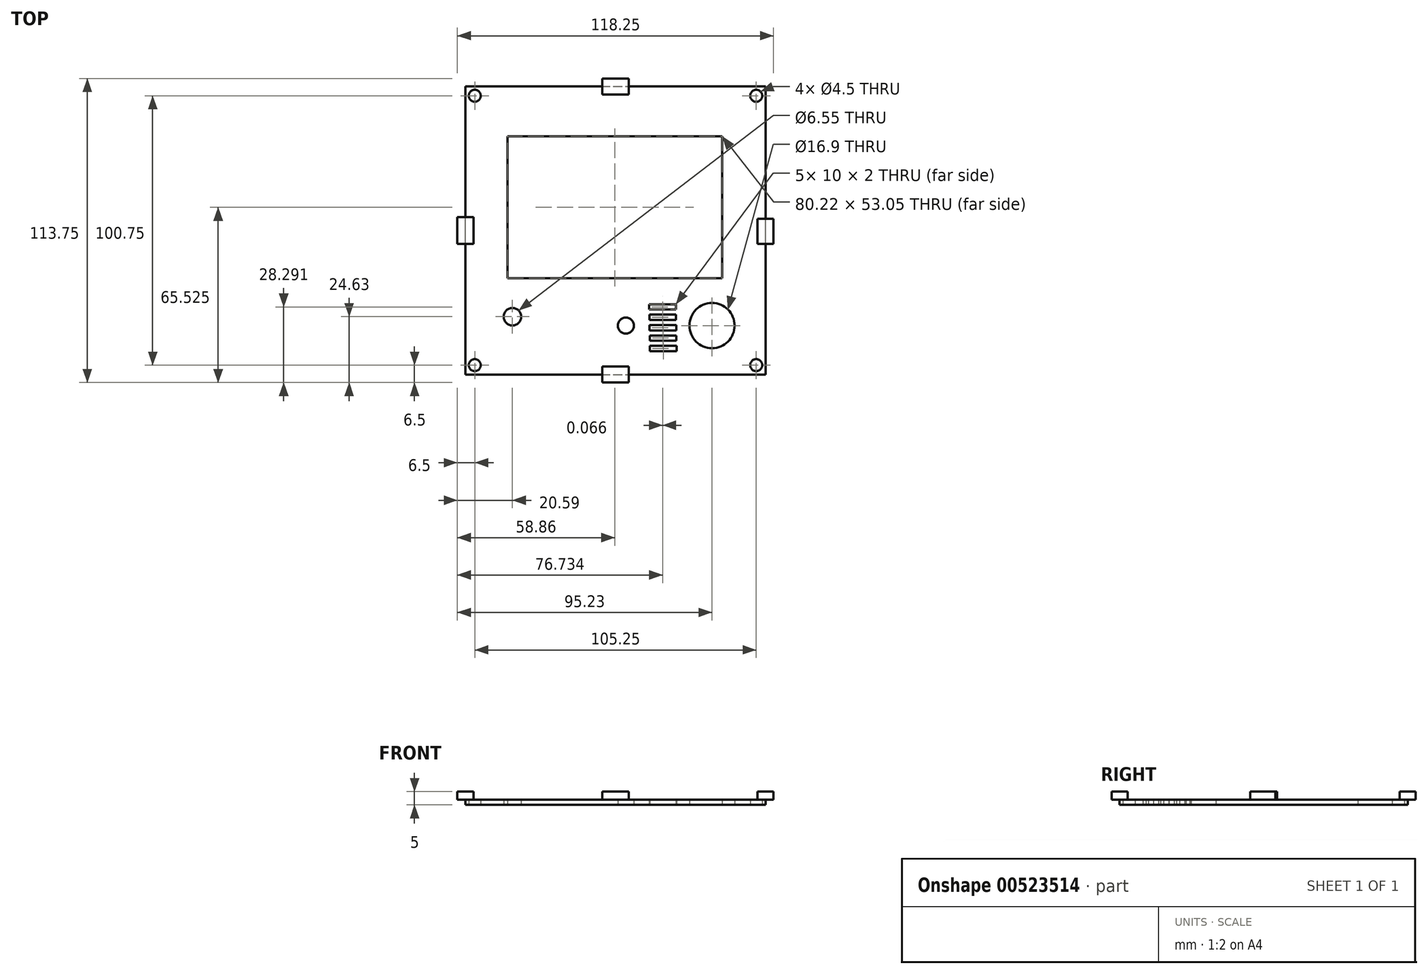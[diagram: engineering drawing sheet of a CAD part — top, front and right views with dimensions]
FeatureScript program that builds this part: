
annotation { "Feature Type Name" : "Feature", "Feature Type Description" : "" }
export const myFeature = defineFeature(function(context is Context, id is Id, definition is map)
    precondition{}
    {
        {
            var Q0;
            Q0=qCreatedBy(makeId("Top.planeOp"),FACE);
            var sketch = newSketch(context, id + "F0", { "sketchPlane" : qUnion([Q0])});
            skLineSegment(sketch, "E0.bottom", {"start": v(0, 0) * mm, "end": v(112.25, 0) * mm});
            skLineSegment(sketch, "E0.top", {"start": v(0, 107.75) * mm, "end": v(112.25, 107.75) * mm});
            skLineSegment(sketch, "E0.left", {"start": v(0, 0) * mm, "end": v(0, 107.75) * mm});
            skLineSegment(sketch, "E0.right", {"start": v(112.25, 0) * mm, "end": v(112.25, 107.75) * mm});
            skCircle(sketch, "E1", {"center": v(3.5, 104.25) * mm, "radius": 2.25 * mm});
            skCircle(sketch, "E2", {"center": v(108.75, 104.25) * mm, "radius": 2.25 * mm});
            skCircle(sketch, "E3", {"center": v(3.5, 3.5) * mm, "radius": 2.25 * mm});
            skCircle(sketch, "E4", {"center": v(108.75, 3.5) * mm, "radius": 2.25 * mm});
            skLineSegment(sketch, "E5.bottom", {"start": v(15.75, 89.05) * mm, "end": v(95.97, 89.05) * mm});
            skLineSegment(sketch, "E5.top", {"start": v(15.75, 36) * mm, "end": v(95.97, 36) * mm});
            skLineSegment(sketch, "E5.left", {"start": v(15.75, 89.05) * mm, "end": v(15.75, 36) * mm});
            skLineSegment(sketch, "E5.right", {"start": v(95.97, 89.05) * mm, "end": v(95.97, 36) * mm});
            skCircle(sketch, "E6", {"center": v(92.23, 18.3) * mm, "radius": 8.45 * mm});
            skCircle(sketch, "E7", {"center": v(60, 18.3) * mm, "radius": 3 * mm});
            skCircle(sketch, "E8", {"center": v(17.59, 21.63) * mm, "radius": 3.28 * mm});
            skLineSegment(sketch, "E9.bottom", {"start": v(68.73, 26.3) * mm, "end": v(78.73, 26.3) * mm});
            skLineSegment(sketch, "E9.top", {"start": v(68.73, 24.3) * mm, "end": v(78.73, 24.3) * mm});
            skLineSegment(sketch, "E9.left", {"start": v(68.73, 26.3) * mm, "end": v(68.73, 24.3) * mm});
            skLineSegment(sketch, "E9.right", {"start": v(78.73, 26.3) * mm, "end": v(78.73, 24.3) * mm});
            skLineSegment(sketch, "E10.1.0.0", {"start": v(78.8, 22.4) * mm, "end": v(78.8, 20.4) * mm});
            skLineSegment(sketch, "E10.1.0.1", {"start": v(68.8, 22.4) * mm, "end": v(68.8, 20.4) * mm});
            skLineSegment(sketch, "E10.1.0.2", {"start": v(68.8, 22.4) * mm, "end": v(78.8, 22.4) * mm});
            skLineSegment(sketch, "E10.1.0.3", {"start": v(68.8, 20.4) * mm, "end": v(78.8, 20.4) * mm});
            skLineSegment(sketch, "E10.2.0.0", {"start": v(78.87, 18.5) * mm, "end": v(78.87, 16.5) * mm});
            skLineSegment(sketch, "E10.2.0.1", {"start": v(68.87, 18.5) * mm, "end": v(68.87, 16.5) * mm});
            skLineSegment(sketch, "E10.2.0.2", {"start": v(68.87, 18.5) * mm, "end": v(78.87, 18.5) * mm});
            skLineSegment(sketch, "E10.2.0.3", {"start": v(68.87, 16.5) * mm, "end": v(78.87, 16.5) * mm});
            skLineSegment(sketch, "E10.3.0.0", {"start": v(78.93, 14.62) * mm, "end": v(78.93, 12.62) * mm});
            skLineSegment(sketch, "E10.3.0.1", {"start": v(68.93, 14.62) * mm, "end": v(68.93, 12.62) * mm});
            skLineSegment(sketch, "E10.3.0.2", {"start": v(68.93, 14.62) * mm, "end": v(78.93, 14.62) * mm});
            skLineSegment(sketch, "E10.3.0.3", {"start": v(68.93, 12.62) * mm, "end": v(78.93, 12.62) * mm});
            skLineSegment(sketch, "E10.4.0.0", {"start": v(79, 10.73) * mm, "end": v(79, 8.73) * mm});
            skLineSegment(sketch, "E10.4.0.1", {"start": v(69, 10.73) * mm, "end": v(69, 8.73) * mm});
            skLineSegment(sketch, "E10.4.0.2", {"start": v(69, 10.73) * mm, "end": v(79, 10.73) * mm});
            skLineSegment(sketch, "E10.4.0.3", {"start": v(69, 8.73) * mm, "end": v(79, 8.73) * mm});
            skLineSegment(sketch, "E10.direction1", {"start": v(68.73, 24.3) * mm, "end": v(68.8, 20.4) * mm, "construction": true});
            skSolve(sketch);
        }
        {
            var Q0;
            Q0 = qSketchRegion(id + "F0", true);
            extrude(context, id + "F1", {"entities" : qUnion([Q0]), "depth" : 2 * mm, "offsetDistance" : 25 * mm});
        }
        {
            var Q0;
            Q0=makeQuery(id+"F1.opExtrude","CAP_FACE",FACE,{"disambiguationData":[OSD([sQuery(id+"F0.wireOp",EDGE,"E0.bottom"),sQuery(id+"F0.wireOp",EDGE,"E0.top"),sQuery(id+"F0.wireOp",EDGE,"E0.left"),sQuery(id+"F0.wireOp",EDGE,"E0.right"),sQuery(id+"F0.wireOp",EDGE,"E1"),sQuery(id+"F0.wireOp",EDGE,"E2"),sQuery(id+"F0.wireOp",EDGE,"E3"),sQuery(id+"F0.wireOp",EDGE,"E4"),sQuery(id+"F0.wireOp",EDGE,"E5.bottom"),sQuery(id+"F0.wireOp",EDGE,"E5.top"),sQuery(id+"F0.wireOp",EDGE,"E5.left"),sQuery(id+"F0.wireOp",EDGE,"E5.right"),sQuery(id+"F0.wireOp",EDGE,"E6"),sQuery(id+"F0.wireOp",EDGE,"E7"),sQuery(id+"F0.wireOp",EDGE,"E8"),sQuery(id+"F0.wireOp",EDGE,"E9.bottom"),sQuery(id+"F0.wireOp",EDGE,"E9.top"),sQuery(id+"F0.wireOp",EDGE,"E9.left"),sQuery(id+"F0.wireOp",EDGE,"E9.right"),sQuery(id+"F0.wireOp",EDGE,"E10.1.0.0"),sQuery(id+"F0.wireOp",EDGE,"E10.1.0.1"),sQuery(id+"F0.wireOp",EDGE,"E10.1.0.2"),sQuery(id+"F0.wireOp",EDGE,"E10.1.0.3"),sQuery(id+"F0.wireOp",EDGE,"E10.2.0.0"),sQuery(id+"F0.wireOp",EDGE,"E10.2.0.1"),sQuery(id+"F0.wireOp",EDGE,"E10.2.0.2"),sQuery(id+"F0.wireOp",EDGE,"E10.2.0.3"),sQuery(id+"F0.wireOp",EDGE,"E10.3.0.0"),sQuery(id+"F0.wireOp",EDGE,"E10.3.0.1"),sQuery(id+"F0.wireOp",EDGE,"E10.3.0.2"),sQuery(id+"F0.wireOp",EDGE,"E10.3.0.3"),sQuery(id+"F0.wireOp",EDGE,"E10.4.0.0"),sQuery(id+"F0.wireOp",EDGE,"E10.4.0.1"),sQuery(id+"F0.wireOp",EDGE,"E10.4.0.2"),sQuery(id+"F0.wireOp",EDGE,"E10.4.0.3")])],"isStart":false});
            var sketch = newSketch(context, id + "F2", { "sketchPlane" : qUnion([Q0])});
            skLineSegment(sketch, "E11.bottom", {"start": v(109.25, 58.25) * mm, "end": v(115.25, 58.25) * mm});
            skLineSegment(sketch, "E11.top", {"start": v(109.25, 48.87) * mm, "end": v(115.25, 48.87) * mm});
            skLineSegment(sketch, "E11.left", {"start": v(109.25, 58.25) * mm, "end": v(109.25, 48.87) * mm});
            skLineSegment(sketch, "E11.right", {"start": v(115.25, 58.25) * mm, "end": v(115.25, 48.87) * mm});
            skLineSegment(sketch, "E12.bottom", {"start": v(-3, 58.87) * mm, "end": v(3, 58.87) * mm});
            skLineSegment(sketch, "E12.top", {"start": v(-3, 48.87) * mm, "end": v(3, 48.87) * mm});
            skLineSegment(sketch, "E12.left", {"start": v(-3, 58.87) * mm, "end": v(-3, 48.87) * mm});
            skLineSegment(sketch, "E12.right", {"start": v(3, 58.87) * mm, "end": v(3, 48.87) * mm});
            skLineSegment(sketch, "E13.bottom", {"start": v(51.13, 110.75) * mm, "end": v(61.13, 110.75) * mm});
            skLineSegment(sketch, "E13.top", {"start": v(51.13, 104.75) * mm, "end": v(61.13, 104.75) * mm});
            skLineSegment(sketch, "E13.left", {"start": v(51.13, 110.75) * mm, "end": v(51.13, 104.75) * mm});
            skLineSegment(sketch, "E13.right", {"start": v(61.13, 110.75) * mm, "end": v(61.13, 104.75) * mm});
            skLineSegment(sketch, "E14.bottom", {"start": v(51.13, 3) * mm, "end": v(61.13, 3) * mm});
            skLineSegment(sketch, "E14.top", {"start": v(51.13, -3) * mm, "end": v(61.13, -3) * mm});
            skLineSegment(sketch, "E14.left", {"start": v(51.13, 3) * mm, "end": v(51.13, -3) * mm});
            skLineSegment(sketch, "E14.right", {"start": v(61.13, 3) * mm, "end": v(61.13, -3) * mm});
            skSolve(sketch);
        }
        {
            var Q0;
            Q0 = qSketchRegion(id + "F2", true);
            extrude(context, id + "F3", {"entities" : qUnion([Q0]), "operationType" : NewBodyOperationType.ADD, "depth" : 3 * mm, "offsetDistance" : 25 * mm});
        }
    });
